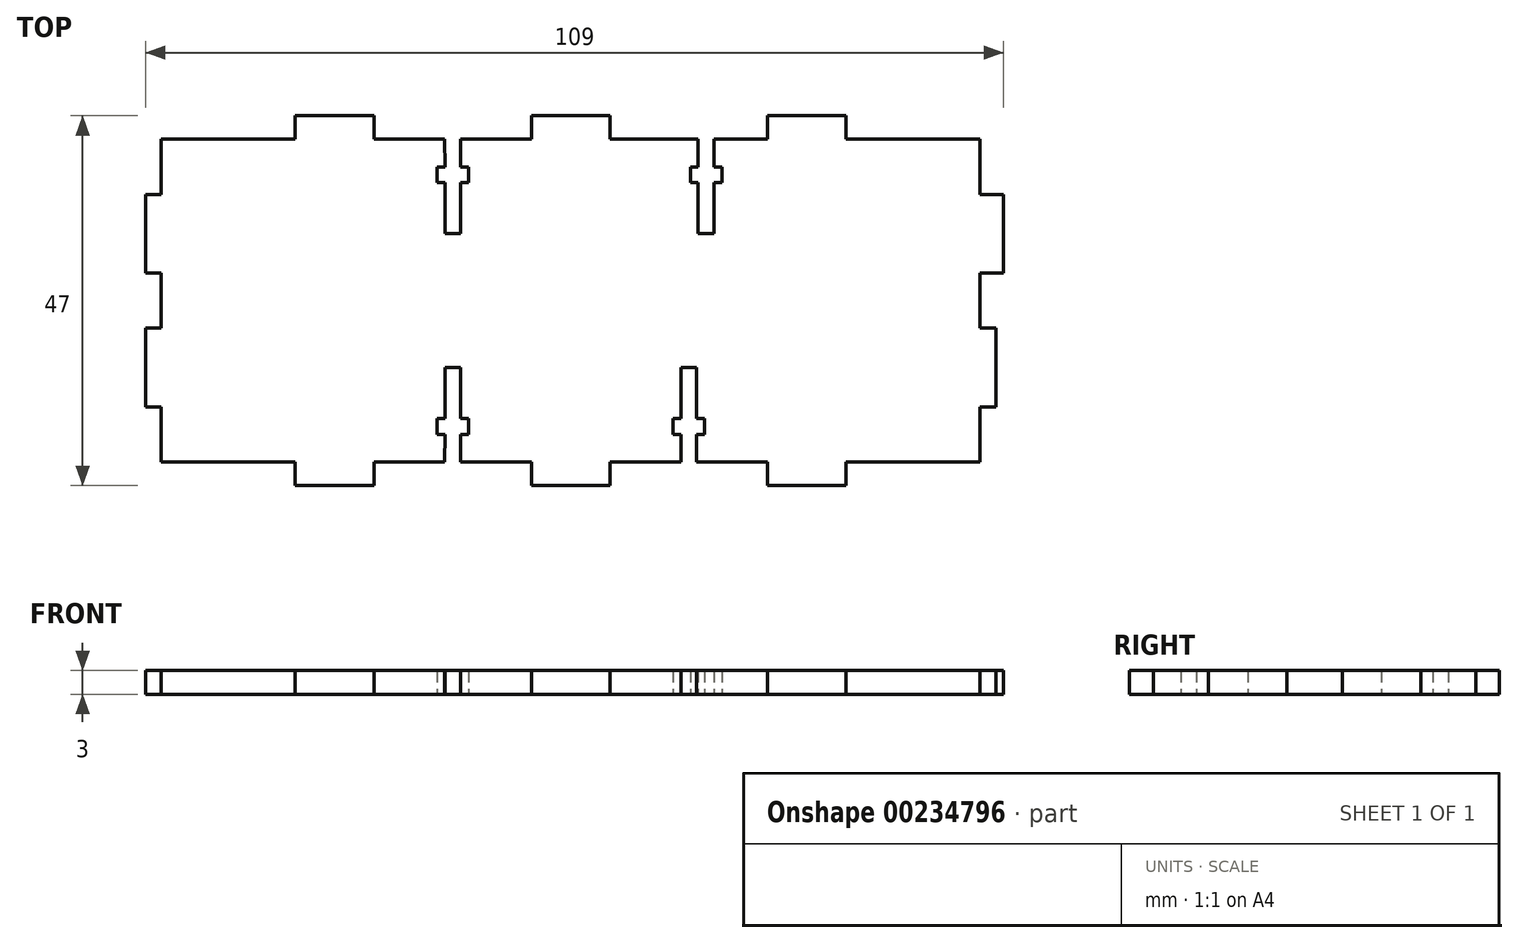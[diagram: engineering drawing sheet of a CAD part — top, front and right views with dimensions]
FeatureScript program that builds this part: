
annotation { "Feature Type Name" : "Feature", "Feature Type Description" : "" }
export const myFeature = defineFeature(function(context is Context, id is Id, definition is map)
    precondition{}
    {
        {
            var Q0;
            Q0=qCreatedBy(makeId("Top.planeOp"),FACE);
            var sketch = newSketch(context, id + "F0", { "sketchPlane" : qUnion([Q0])});
            skLineSegment(sketch, "E0.bottom", {"start": v(-52.22, 20.56) * mm, "end": v(-35.22, 20.56) * mm});
            skLineSegment(sketch, "E0.left", {"start": v(-52.22, 20.56) * mm, "end": v(-52.22, 13.56) * mm});
            skLineSegment(sketch, "E0.right", {"start": v(51.78, 20.56) * mm, "end": v(51.78, 13.56) * mm});
            skPoint(sketch, "E1", {"position": v(17.32, 78.75) * mm});
            skLineSegment(sketch, "E2", {"start": v(-35.22, 20.56) * mm, "end": v(-35.22, 23.56) * mm});
            skLineSegment(sketch, "E3", {"start": v(-35.22, 23.56) * mm, "end": v(-25.22, 23.56) * mm});
            skLineSegment(sketch, "E4", {"start": v(-25.22, 23.56) * mm, "end": v(-25.22, 20.56) * mm});
            skLineSegment(sketch, "E5", {"start": v(-5.22, 20.56) * mm, "end": v(-5.22, 23.56) * mm});
            skLineSegment(sketch, "E6", {"start": v(-5.22, 23.56) * mm, "end": v(4.78, 23.56) * mm});
            skLineSegment(sketch, "E7", {"start": v(4.78, 23.56) * mm, "end": v(4.78, 20.56) * mm});
            skLineSegment(sketch, "E8", {"start": v(24.78, 20.56) * mm, "end": v(24.78, 23.56) * mm});
            skLineSegment(sketch, "E9", {"start": v(24.78, 23.56) * mm, "end": v(34.78, 23.56) * mm});
            skLineSegment(sketch, "E10", {"start": v(34.78, 23.56) * mm, "end": v(34.78, 20.56) * mm});
            skLineSegment(sketch, "E11", {"start": v(15.97, 20.56) * mm, "end": v(15.97, 17.06) * mm});
            skLineSegment(sketch, "E12", {"start": v(15.97, 17.06) * mm, "end": v(14.97, 17.06) * mm});
            skLineSegment(sketch, "E13", {"start": v(14.97, 17.06) * mm, "end": v(14.97, 15.06) * mm});
            skLineSegment(sketch, "E14", {"start": v(14.97, 15.06) * mm, "end": v(15.97, 15.06) * mm});
            skLineSegment(sketch, "E15", {"start": v(15.97, 15.06) * mm, "end": v(15.97, 8.56) * mm});
            skLineSegment(sketch, "E16", {"start": v(17.97, 17.06) * mm, "end": v(17.97, 20.56) * mm});
            skLineSegment(sketch, "E17.trimOffspring", {"start": v(17.97, 20.56) * mm, "end": v(24.78, 20.56) * mm});
            skLineSegment(sketch, "E18", {"start": v(15.97, 8.56) * mm, "end": v(17.97, 8.56) * mm});
            skLineSegment(sketch, "E19", {"start": v(17.97, 8.56) * mm, "end": v(17.97, 15.06) * mm});
            skLineSegment(sketch, "E20", {"start": v(-17.2, 17.06) * mm, "end": v(-17.2, 15.06) * mm});
            skLineSegment(sketch, "E21", {"start": v(-17.2, 15.06) * mm, "end": v(-16.2, 15.06) * mm});
            skLineSegment(sketch, "E22", {"start": v(-16.2, 15.06) * mm, "end": v(-16.2, 8.56) * mm});
            skLineSegment(sketch, "E23.MirrorCS", {"start": v(-13.2, 15.06) * mm, "end": v(-14.2, 15.06) * mm});
            skLineSegment(sketch, "E24.MirrorCS", {"start": v(-13.2, 17.06) * mm, "end": v(-13.2, 15.06) * mm});
            skLineSegment(sketch, "E25", {"start": v(-16.2, 8.56) * mm, "end": v(-14.2, 8.56) * mm});
            skLineSegment(sketch, "E26", {"start": v(-14.2, 8.56) * mm, "end": v(-14.2, 15.06) * mm});
            skLineSegment(sketch, "E27.trimOffspring", {"start": v(-14.2, 20.56) * mm, "end": v(-5.22, 20.56) * mm});
            skLineSegment(sketch, "E28.trimOffspring", {"start": v(4.78, 20.56) * mm, "end": v(15.97, 20.56) * mm});
            skLineSegment(sketch, "E29.trimOffspring", {"start": v(34.78, 20.56) * mm, "end": v(51.78, 20.56) * mm});
            skLineSegment(sketch, "E30.trimOffspring", {"start": v(-25.22, 20.56) * mm, "end": v(-16.22, 20.56) * mm});
            skLineSegment(sketch, "E31", {"start": v(-52.22, 13.56) * mm, "end": v(-54.22, 13.56) * mm});
            skLineSegment(sketch, "E32", {"start": v(-54.22, 13.56) * mm, "end": v(-54.22, 3.56) * mm});
            skLineSegment(sketch, "E33", {"start": v(-54.22, 3.56) * mm, "end": v(-52.22, 3.56) * mm});
            skLineSegment(sketch, "E34.trimOffspring", {"start": v(-52.22, 3.56) * mm, "end": v(-52.22, 0.06) * mm});
            skLineSegment(sketch, "E35", {"start": v(51.78, 3.56) * mm, "end": v(54.78, 3.56) * mm});
            skLineSegment(sketch, "E36", {"start": v(54.78, 3.56) * mm, "end": v(54.78, 13.56) * mm});
            skLineSegment(sketch, "E37", {"start": v(54.78, 13.56) * mm, "end": v(51.78, 13.56) * mm});
            skLineSegment(sketch, "E38.trimOffspring", {"start": v(51.78, 3.56) * mm, "end": v(51.78, 0.06) * mm});
            skLineSegment(sketch, "E39", {"start": v(-17.2, 17.06) * mm, "end": v(-16.2, 17.06) * mm});
            skLineSegment(sketch, "E40", {"start": v(-14.2, 20.56) * mm, "end": v(-14.2, 17.06) * mm});
            skLineSegment(sketch, "E41", {"start": v(-14.2, 17.06) * mm, "end": v(-13.2, 17.06) * mm});
            skLineSegment(sketch, "E42", {"start": v(17.97, 17.06) * mm, "end": v(18.97, 17.06) * mm});
            skLineSegment(sketch, "E43", {"start": v(18.97, 17.06) * mm, "end": v(18.97, 15.06) * mm});
            skLineSegment(sketch, "E44", {"start": v(18.97, 15.06) * mm, "end": v(17.97, 15.06) * mm});
            skLineSegment(sketch, "E45", {"start": v(-16.22, 20.56) * mm, "end": v(-16.2, 17.06) * mm});
            skLineSegment(sketch, "E46.MirrorCS", {"start": v(-14.22, -16.94) * mm, "end": v(-13.22, -16.94) * mm});
            skLineSegment(sketch, "E47.MirrorCS", {"start": v(-17.2, -16.94) * mm, "end": v(-17.2, -14.94) * mm});
            skLineSegment(sketch, "E48.MirrorCS", {"start": v(-13.22, -16.94) * mm, "end": v(-13.22, -14.94) * mm});
            skLineSegment(sketch, "E49.MirrorCS", {"start": v(-13.22, -14.94) * mm, "end": v(-14.2, -14.94) * mm});
            skLineSegment(sketch, "E50.MirrorCS", {"start": v(-17.2, -16.94) * mm, "end": v(-16.2, -16.94) * mm});
            skLineSegment(sketch, "E51.MirrorCS", {"start": v(12.78, -14.94) * mm, "end": v(13.78, -14.94) * mm});
            skLineSegment(sketch, "E52.MirrorCS", {"start": v(15.78, -16.94) * mm, "end": v(16.78, -16.94) * mm});
            skLineSegment(sketch, "E53.MirrorCS", {"start": v(12.78, -16.94) * mm, "end": v(12.78, -14.94) * mm});
            skLineSegment(sketch, "E54.MirrorCS", {"start": v(13.78, -16.94) * mm, "end": v(12.78, -16.94) * mm});
            skLineSegment(sketch, "E55.MirrorCS", {"start": v(-17.2, -14.94) * mm, "end": v(-16.2, -14.94) * mm});
            skLineSegment(sketch, "E56.MirrorCS", {"start": v(16.78, -16.94) * mm, "end": v(16.78, -14.94) * mm});
            skLineSegment(sketch, "E57.MirrorCS", {"start": v(16.78, -14.94) * mm, "end": v(15.78, -14.94) * mm});
            skLineSegment(sketch, "E58.MirrorCS", {"start": v(51.78, -3.44) * mm, "end": v(53.78, -3.44) * mm});
            skLineSegment(sketch, "E59.MirrorCS", {"start": v(-52.22, -13.44) * mm, "end": v(-54.22, -13.44) * mm});
            skLineSegment(sketch, "E60.MirrorCS", {"start": v(34.78, -23.44) * mm, "end": v(34.78, -20.44) * mm});
            skLineSegment(sketch, "E61.MirrorCS", {"start": v(24.78, -20.44) * mm, "end": v(24.78, -23.44) * mm});
            skLineSegment(sketch, "E62.MirrorCS", {"start": v(4.78, -23.44) * mm, "end": v(4.78, -20.44) * mm});
            skLineSegment(sketch, "E63.MirrorCS", {"start": v(-5.22, -20.44) * mm, "end": v(-5.22, -23.44) * mm});
            skLineSegment(sketch, "E64.MirrorCS", {"start": v(-25.22, -23.44) * mm, "end": v(-25.22, -20.44) * mm});
            skLineSegment(sketch, "E65.MirrorCS", {"start": v(-35.22, -20.44) * mm, "end": v(-35.22, -23.44) * mm});
            skLineSegment(sketch, "E66.MirrorCS", {"start": v(13.78, -8.44) * mm, "end": v(15.78, -8.44) * mm});
            skLineSegment(sketch, "E67.MirrorCS", {"start": v(-16.2, -8.44) * mm, "end": v(-14.2, -8.44) * mm});
            skLineSegment(sketch, "E68.MirrorCS", {"start": v(53.78, -13.44) * mm, "end": v(51.78, -13.44) * mm});
            skLineSegment(sketch, "E69.MirrorCS", {"start": v(-54.22, -3.44) * mm, "end": v(-52.22, -3.44) * mm});
            skLineSegment(sketch, "E70.MirrorCS", {"start": v(-14.22, -20.44) * mm, "end": v(-14.22, -16.94) * mm});
            skLineSegment(sketch, "E71.MirrorCS", {"start": v(15.78, -16.94) * mm, "end": v(15.78, -20.44) * mm});
            skLineSegment(sketch, "E72.MirrorCS", {"start": v(13.78, -20.44) * mm, "end": v(13.78, -16.94) * mm});
            skLineSegment(sketch, "E73.MirrorCS", {"start": v(-16.22, -20.44) * mm, "end": v(-16.2, -16.94) * mm});
            skLineSegment(sketch, "E74.MirrorCS", {"start": v(15.78, -8.44) * mm, "end": v(15.78, -14.94) * mm});
            skLineSegment(sketch, "E75.MirrorCS", {"start": v(-14.22, -20.44) * mm, "end": v(-5.22, -20.44) * mm});
            skLineSegment(sketch, "E76.MirrorCS", {"start": v(15.78, -20.44) * mm, "end": v(24.78, -20.44) * mm});
            skLineSegment(sketch, "E77.MirrorCS", {"start": v(-14.2, -8.44) * mm, "end": v(-14.2, -14.94) * mm});
            skLineSegment(sketch, "E78.MirrorCS", {"start": v(-52.22, -3.44) * mm, "end": v(-52.22, 0.12) * mm});
            skLineSegment(sketch, "E79.MirrorCS", {"start": v(-54.22, -13.44) * mm, "end": v(-54.22, -3.44) * mm});
            skLineSegment(sketch, "E80.MirrorCS", {"start": v(4.78, -20.44) * mm, "end": v(13.78, -20.44) * mm});
            skLineSegment(sketch, "E81.MirrorCS", {"start": v(13.78, -14.94) * mm, "end": v(13.78, -8.44) * mm});
            skLineSegment(sketch, "E82.MirrorCS", {"start": v(-16.2, -14.94) * mm, "end": v(-16.2, -8.44) * mm});
            skLineSegment(sketch, "E83.MirrorCS", {"start": v(24.78, -23.44) * mm, "end": v(34.78, -23.44) * mm});
            skLineSegment(sketch, "E84.MirrorCS", {"start": v(-5.22, -23.44) * mm, "end": v(4.78, -23.44) * mm});
            skLineSegment(sketch, "E85.MirrorCS", {"start": v(-35.22, -23.44) * mm, "end": v(-25.22, -23.44) * mm});
            skLineSegment(sketch, "E86.MirrorCS", {"start": v(51.78, -20.44) * mm, "end": v(51.78, -13.44) * mm});
            skLineSegment(sketch, "E87.MirrorCS", {"start": v(-52.22, -20.44) * mm, "end": v(-52.22, -13.44) * mm});
            skLineSegment(sketch, "E88.MirrorCS", {"start": v(-52.22, -20.44) * mm, "end": v(-35.22, -20.44) * mm});
            skLineSegment(sketch, "E89.MirrorCS", {"start": v(-25.22, -20.44) * mm, "end": v(-16.22, -20.44) * mm});
            skLineSegment(sketch, "E90.MirrorCS", {"start": v(53.78, -3.44) * mm, "end": v(53.78, -13.44) * mm});
            skLineSegment(sketch, "E91.MirrorCS", {"start": v(51.78, -3.44) * mm, "end": v(51.78, 0.06) * mm});
            skLineSegment(sketch, "E92.MirrorCS", {"start": v(34.78, -20.44) * mm, "end": v(51.78, -20.44) * mm});
            skSolve(sketch);
        }
        {
            var Q0;
            Q0=makeQuery(id+"F0.imprint","IMPRINT",FACE,{"disambiguationData":[TD([[makeQuery(id+"F0.imprint","IMPRINT",EDGE,{"derivedFrom":sQuery(id+"F0.wireOp",EDGE,"E0.bottom")}),-1.0]])]});
            extrude(context, id + "F1", {"entities" : qUnion([Q0]), "endBound" : BoundingType.SYMMETRIC, "depth" : 3 * mm});
        }
    });
